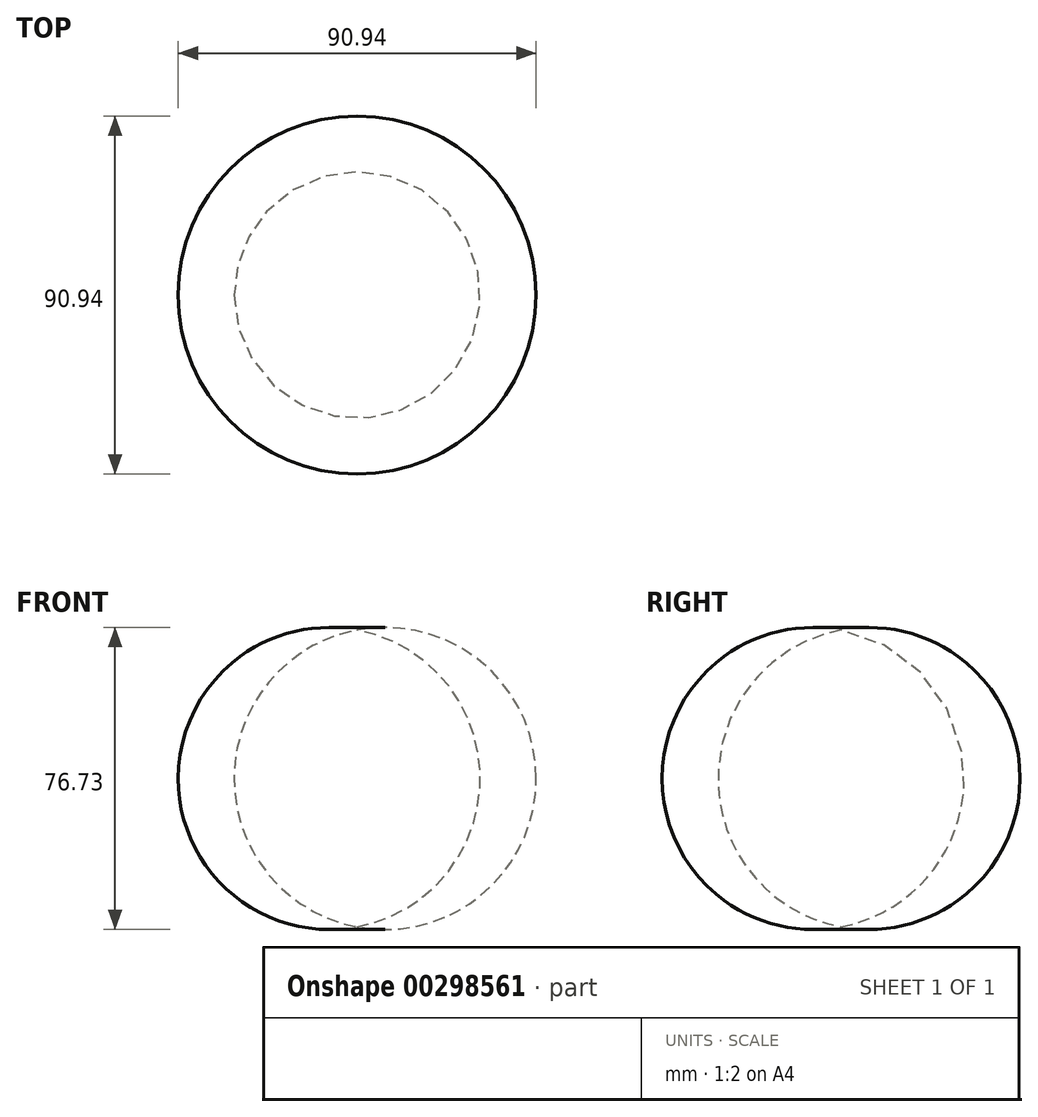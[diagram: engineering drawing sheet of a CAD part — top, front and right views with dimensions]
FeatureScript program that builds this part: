
annotation { "Feature Type Name" : "Feature", "Feature Type Description" : "" }
export const myFeature = defineFeature(function(context is Context, id is Id, definition is map)
    precondition{}
    {
        {
            var Q0;
            Q0=qCreatedBy(makeId("Front.planeOp"),FACE);
            var sketch = newSketch(context, id + "F0", { "sketchPlane" : qUnion([Q0])});
            skArc(sketch, "E0", {"start": v(0, 52.19) * mm, "mid": v(-45.47, 14.49) * mm, "end": v(0, -23.22) * mm});
            skLineSegment(sketch, "E1", {"start": v(0, 52.19) * mm, "end": v(0, -23.22) * mm});
            skSolve(sketch);
        }
        {
            var Q0;
            Q0=makeQuery(id+"F0.imprint","IMPRINT",FACE,{"disambiguationData":[TD([[makeQuery(id+"F0.imprint","IMPRINT",EDGE,{"derivedFrom":sQuery(id+"F0.wireOp",EDGE,"E0")}),1.0]])]});
            var Q1;
            Q1=sQuery(id+"F0.wireOp",EDGE,"E1");
            revolve(context, id + "F1", {"entities" : qUnion([Q0]), "axis" : qUnion([Q1]), "revolveType" : RevolveType.FULL});
        }
    });
